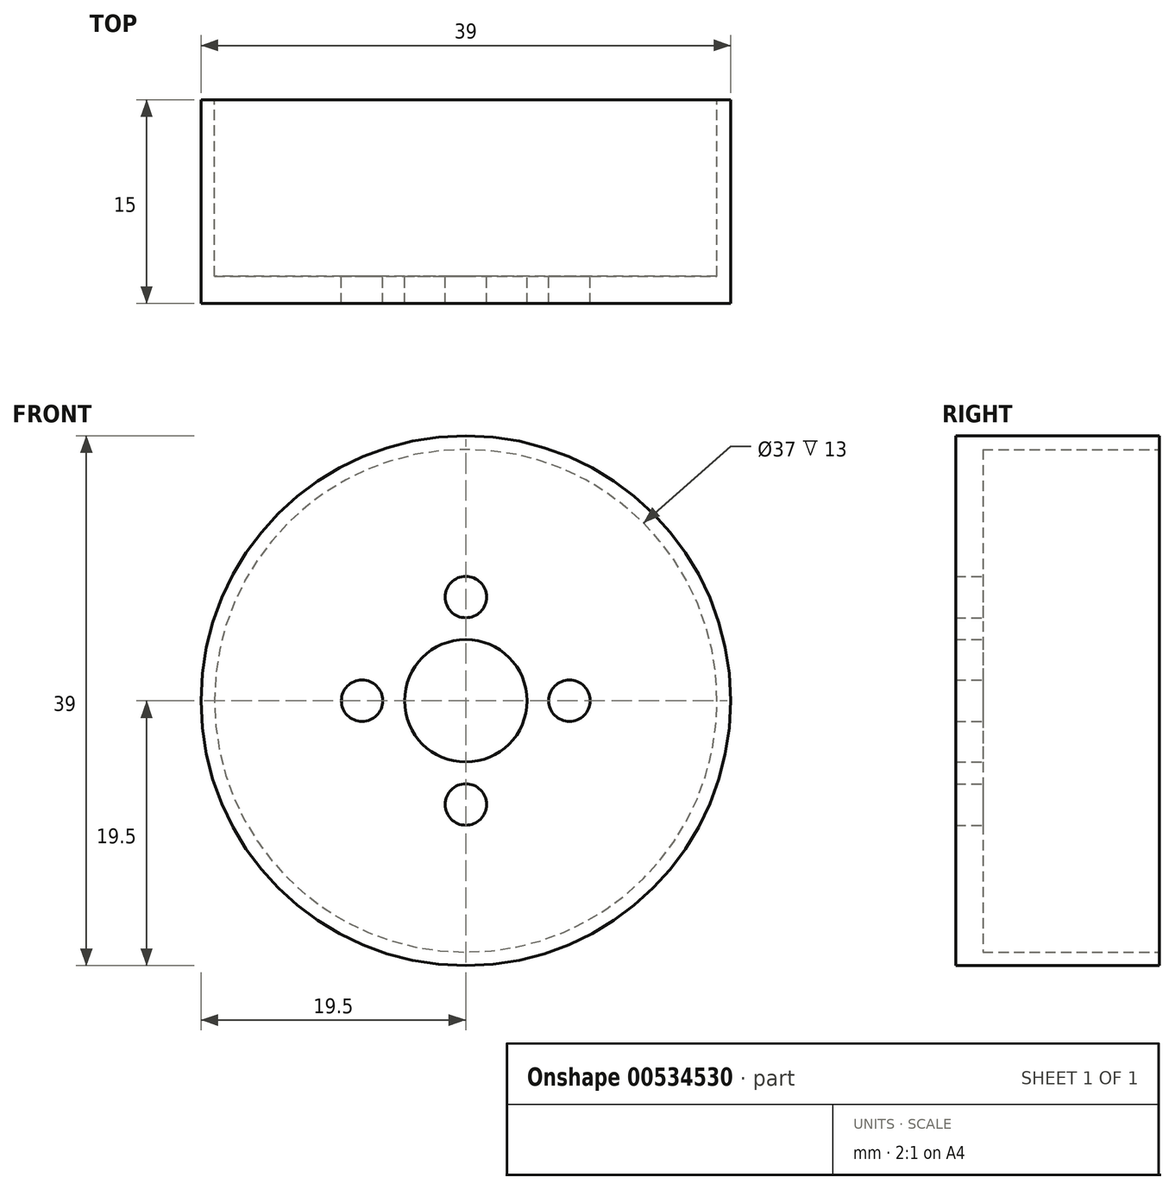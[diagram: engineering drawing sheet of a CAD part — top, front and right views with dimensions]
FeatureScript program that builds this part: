
annotation { "Feature Type Name" : "Feature", "Feature Type Description" : "" }
export const myFeature = defineFeature(function(context is Context, id is Id, definition is map)
    precondition{}
    {
        {
            var Q0;
            Q0=qCreatedBy(makeId("Front.planeOp"),FACE);
            var sketch = newSketch(context, id + "F0", { "sketchPlane" : qUnion([Q0])});
            skCircle(sketch, "E0", {"center": v(0, 0) * mm, "radius": 19.5 * mm});
            skSolve(sketch);
        }
        {
            var Q0;
            Q0=makeQuery(id+"F0.imprint","IMPRINT",FACE,{"disambiguationData":[TD([[makeQuery(id+"F0.imprint","IMPRINT",EDGE,{"derivedFrom":sQuery(id+"F0.wireOp",EDGE,"E0")}),1.0]])]});
            extrude(context, id + "F1", {"entities" : qUnion([Q0]), "depth" : 15 * mm, "offsetDistance" : 25.4 * mm});
        }
        {
            var Q0;
            Q0=makeQuery(id+"F1.opExtrude","CAP_FACE",FACE,{"disambiguationData":[OSD([sQuery(id+"F0.wireOp",EDGE,"E0")])],"isStart":true});
            var sketch = newSketch(context, id + "F2", { "sketchPlane" : qUnion([Q0])});
            skCircle(sketch, "E1", {"center": v(0, 0) * mm, "radius": 18.5 * mm});
            skSolve(sketch);
        }
        {
            var Q0;
            Q0=makeQuery(id+"F2.imprint","IMPRINT",FACE,{"disambiguationData":[TD([[makeQuery(id+"F2.imprint","IMPRINT",EDGE,{"derivedFrom":sQuery(id+"F2.wireOp",EDGE,"E1")}),1.0]])]});
            extrude(context, id + "F3", {"entities" : qUnion([Q0]), "operationType" : NewBodyOperationType.REMOVE, "oppositeDirection" : true, "depth" : 13 * mm, "offsetDistance" : 25.4 * mm});
        }
        {
            var Q0;
            Q0=makeQuery(id+"F3.boolean.opBoolean","COPY",FACE,{"derivedFrom":makeQuery(id+"F3.opExtrude","CAP_FACE",FACE,{"disambiguationData":[OSD([sQuery(id+"F2.wireOp",EDGE,"E1")])],"isStart":false})});
            var sketch = newSketch(context, id + "F4", { "sketchPlane" : qUnion([Q0])});
            skCircle(sketch, "E2", {"center": v(0, 0) * mm, "radius": 4.5 * mm});
            skCircle(sketch, "E3", {"center": v(0, 7.64) * mm, "radius": 1.52 * mm});
            skCircle(sketch, "E4.1.0", {"center": v(-7.64, 0) * mm, "radius": 1.52 * mm});
            skCircle(sketch, "E4.2.0", {"center": v(0, -7.64) * mm, "radius": 1.52 * mm});
            skCircle(sketch, "E4.3.0", {"center": v(7.64, 0) * mm, "radius": 1.52 * mm});
            skSolve(sketch);
        }
        {
            var Q0;
            Q0 = qSketchRegion(id + "F4", true);
            extrude(context, id + "F5", {"entities" : qUnion([Q0]), "operationType" : NewBodyOperationType.REMOVE, "endBound" : BoundingType.THROUGH_ALL, "oppositeDirection" : true, "depth" : 25.4 * mm, "offsetDistance" : 25.4 * mm});
        }
    });
